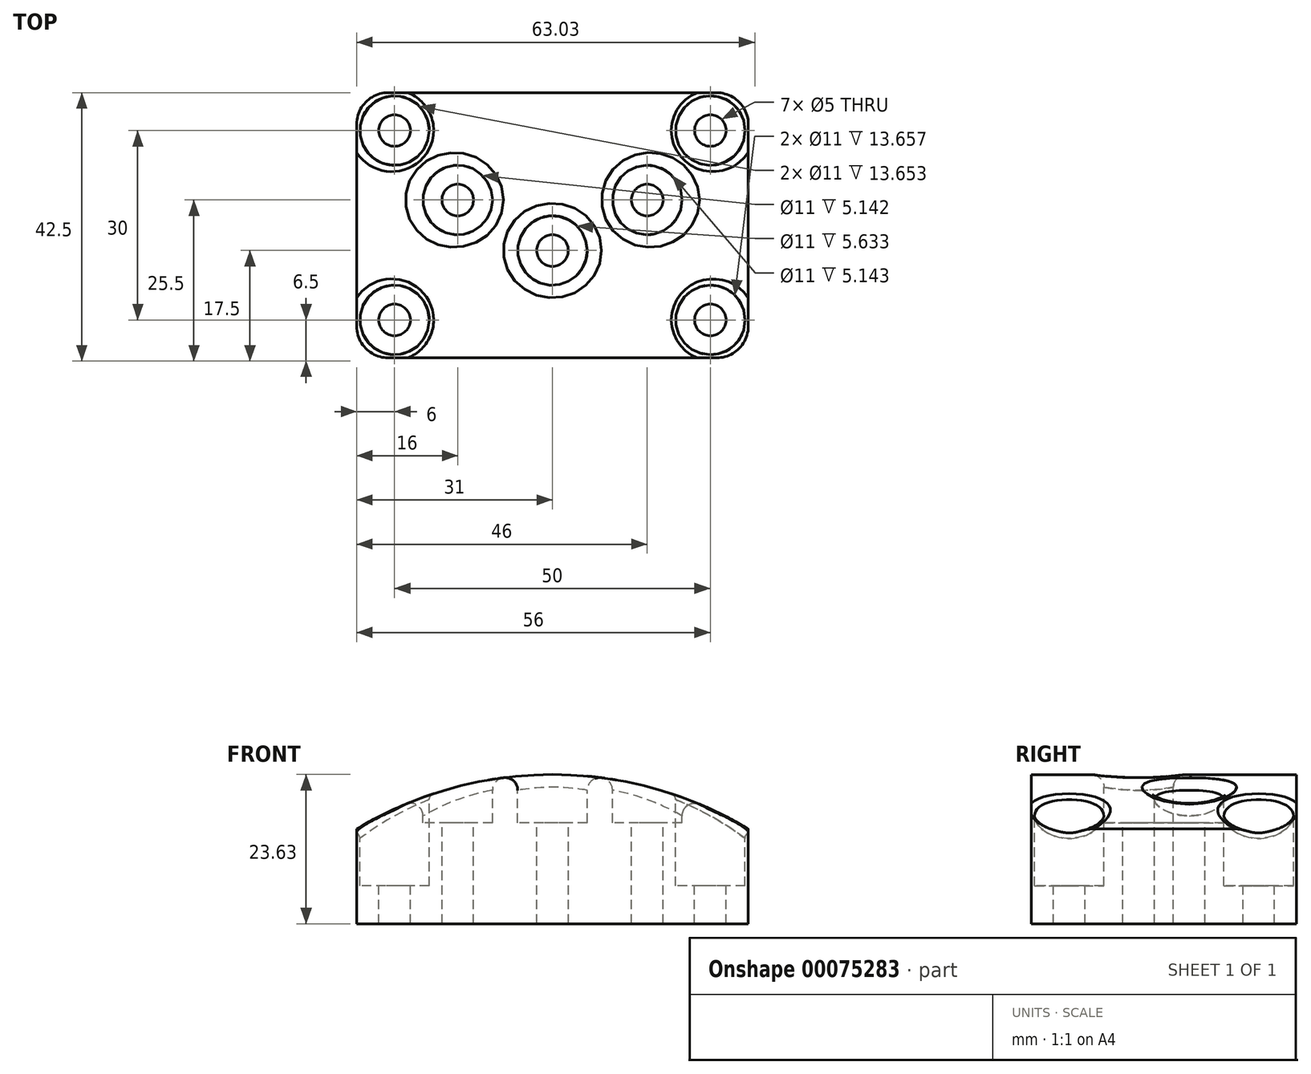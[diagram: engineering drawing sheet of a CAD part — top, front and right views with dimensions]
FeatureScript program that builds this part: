
annotation { "Feature Type Name" : "Feature", "Feature Type Description" : "" }
export const myFeature = defineFeature(function(context is Context, id is Id, definition is map)
    precondition{}
    {
        {
            var Q0;
            Q0=qCreatedBy(makeId("Top.planeOp"),FACE);
            var sketch = newSketch(context, id + "F0", { "sketchPlane" : qUnion([Q0])});
            skLineSegment(sketch, "E0.rect.bottom", {"start": v(-31, 21) * mm, "end": v(31, 21) * mm});
            skLineSegment(sketch, "E0.rect.top", {"start": v(-31, -21) * mm, "end": v(31, -21) * mm});
            skLineSegment(sketch, "E0.rect.left", {"start": v(-31, 21) * mm, "end": v(-31, -21) * mm});
            skLineSegment(sketch, "E0.rect.right", {"start": v(31, 21) * mm, "end": v(31, -21) * mm});
            skPoint(sketch, "E0.rect.middle", {"position": v(0, 0) * mm});
            skSolve(sketch);
        }
        {
            var Q0;
            Q0 = qSketchRegion(id + "F0", true);
            extrude(context, id + "F1", {"entities" : qUnion([Q0]), "depth" : 25 * mm});
        }
        {
            var Q0;
            Q0=makeQuery(id+"F1.opExtrude","CAP_FACE",FACE,{"disambiguationData":[OSD([sQuery(id+"F0.wireOp",EDGE,"E0.rect.bottom"),sQuery(id+"F0.wireOp",EDGE,"E0.rect.top"),sQuery(id+"F0.wireOp",EDGE,"E0.rect.left"),sQuery(id+"F0.wireOp",EDGE,"E0.rect.right")])],"isStart":false});
            var sketch = newSketch(context, id + "F2", { "sketchPlane" : qUnion([Q0])});
            skLineSegment(sketch, "E1", {"start": v(-25, 21) * mm, "end": v(-25, -21) * mm, "construction": true});
            skLineSegment(sketch, "E2", {"start": v(25, 21) * mm, "end": v(25, -21) * mm, "construction": true});
            skLineSegment(sketch, "E3", {"start": v(-31, -15) * mm, "end": v(31, -15) * mm, "construction": true});
            skLineSegment(sketch, "E4", {"start": v(-31, 15) * mm, "end": v(31, 15) * mm, "construction": true});
            skLineSegment(sketch, "E5", {"start": v(-31, 4) * mm, "end": v(31, 4) * mm, "construction": true});
            skLineSegment(sketch, "E6", {"start": v(-31, -4) * mm, "end": v(31, -4) * mm, "construction": true});
            skLineSegment(sketch, "E7", {"start": v(0, 21) * mm, "end": v(0, -21) * mm, "construction": true});
            skLineSegment(sketch, "E8", {"start": v(-15, 21) * mm, "end": v(-15, -21) * mm, "construction": true});
            skLineSegment(sketch, "E9", {"start": v(15, 21) * mm, "end": v(15, -21) * mm, "construction": true});
            skCircle(sketch, "E10", {"center": v(-25, 15) * mm, "radius": 2.5 * mm});
            skCircle(sketch, "E11", {"center": v(-25, -15) * mm, "radius": 2.5 * mm});
            skCircle(sketch, "E12", {"center": v(25, 15) * mm, "radius": 2.5 * mm});
            skCircle(sketch, "E13", {"center": v(0, -4) * mm, "radius": 2.5 * mm});
            skCircle(sketch, "E14", {"center": v(-15, 4) * mm, "radius": 2.5 * mm});
            skCircle(sketch, "E15", {"center": v(15, 4) * mm, "radius": 2.5 * mm});
            skCircle(sketch, "E16", {"center": v(25, -15) * mm, "radius": 2.5 * mm});
            skSolve(sketch);
        }
        {
            var Q0;
            Q0 = qSketchRegion(id + "F2", true);
            var Q1;
            Q1=makeQuery(id+"F1.opExtrude","CAP_FACE",FACE,{"disambiguationData":[OSD([sQuery(id+"F0.wireOp",EDGE,"E0.rect.bottom"),sQuery(id+"F0.wireOp",EDGE,"E0.rect.top"),sQuery(id+"F0.wireOp",EDGE,"E0.rect.left"),sQuery(id+"F0.wireOp",EDGE,"E0.rect.right")])],"isStart":true});
            extrude(context, id + "F3", {"entities" : qUnion([Q0]), "operationType" : NewBodyOperationType.REMOVE, "endBound" : BoundingType.UP_TO_SURFACE, "oppositeDirection" : true, "endBoundEntityFace" : qUnion([Q1]), "depth" : 25 * mm});
        }
        {
            var Q0;
            Q0=makeQuery(id+"F1.opExtrude","CAP_FACE",FACE,{"disambiguationData":[OSD([sQuery(id+"F0.wireOp",EDGE,"E0.rect.bottom"),sQuery(id+"F0.wireOp",EDGE,"E0.rect.top"),sQuery(id+"F0.wireOp",EDGE,"E0.rect.left"),sQuery(id+"F0.wireOp",EDGE,"E0.rect.right")])],"isStart":false});
            var sketch = newSketch(context, id + "F4", { "sketchPlane" : qUnion([Q0])});
            skCircle(sketch, "E17", {"center": v(-15, 4) * mm, "radius": 5.5 * mm});
            skCircle(sketch, "E18", {"center": v(0, -4) * mm, "radius": 5.5 * mm});
            skCircle(sketch, "E19", {"center": v(15, 4) * mm, "radius": 5.5 * mm});
            skSolve(sketch);
        }
        {
            var Q0;
            Q0 = qSketchRegion(id + "F4", true);
            extrude(context, id + "F5", {"entities" : qUnion([Q0]), "operationType" : NewBodyOperationType.REMOVE, "oppositeDirection" : true, "depth" : 9 * mm});
        }
        {
            var Q0;
            Q0=makeQuery(id+"F1.opExtrude","CAP_FACE",FACE,{"disambiguationData":[OSD([sQuery(id+"F0.wireOp",EDGE,"E0.rect.bottom"),sQuery(id+"F0.wireOp",EDGE,"E0.rect.top"),sQuery(id+"F0.wireOp",EDGE,"E0.rect.left"),sQuery(id+"F0.wireOp",EDGE,"E0.rect.right")])],"isStart":false});
            var sketch = newSketch(context, id + "F6", { "sketchPlane" : qUnion([Q0])});
            skCircle(sketch, "E20", {"center": v(-25, 15) * mm, "radius": 5.5 * mm});
            skCircle(sketch, "E21", {"center": v(25, 15) * mm, "radius": 5.5 * mm});
            skCircle(sketch, "E22", {"center": v(25, -15) * mm, "radius": 5.5 * mm});
            skCircle(sketch, "E23", {"center": v(-25, -15) * mm, "radius": 5.5 * mm});
            skSolve(sketch);
        }
        {
            var Q0;
            Q0 = qSketchRegion(id + "F6", true);
            extrude(context, id + "F7", {"entities" : qUnion([Q0]), "operationType" : NewBodyOperationType.REMOVE, "oppositeDirection" : true, "depth" : 19 * mm});
        }
        {
            var Q0;
            Q0=makeQuery(id+"F1.opExtrude","SWEPT_FACE",FACE,{"disambiguationData":[OSD([sQuery(id+"F0.wireOp",EDGE,"E0.rect.top")])]});
            var sketch = newSketch(context, id + "F8", { "sketchPlane" : qUnion([Q0])});
            skArc(sketch, "E24", {"start": v(31, 15) * mm, "mid": v(0, 23.63) * mm, "end": v(-31, 15) * mm});
            skLineSegment(sketch, "E25", {"start": v(-31, 15) * mm, "end": v(-53.05, 15) * mm});
            skLineSegment(sketch, "E26", {"start": v(-53.05, 15) * mm, "end": v(-53.05, 56.68) * mm});
            skLineSegment(sketch, "E27", {"start": v(-53.05, 56.68) * mm, "end": v(46.39, 56.68) * mm});
            skLineSegment(sketch, "E28", {"start": v(46.39, 56.68) * mm, "end": v(46.39, 15) * mm});
            skLineSegment(sketch, "E29", {"start": v(46.39, 15) * mm, "end": v(31, 15) * mm});
            skSolve(sketch);
        }
        {
            var Q0;
            Q0 = qSketchRegion(id + "F8", true);
            var Q1;
            Q1=makeQuery(id+"F1.opExtrude","SWEPT_FACE",FACE,{"disambiguationData":[OSD([sQuery(id+"F0.wireOp",EDGE,"E0.rect.bottom")])]});
            extrude(context, id + "F9", {"entities" : qUnion([Q0]), "operationType" : NewBodyOperationType.REMOVE, "endBound" : BoundingType.UP_TO_SURFACE, "oppositeDirection" : true, "endBoundEntityFace" : qUnion([Q1]), "depth" : 25 * mm});
        }
        {
            var Q0;
            Q0=makeQuery(id+"F1.opExtrude","SWEPT_EDGE",EDGE,{"disambiguationData":[OSD([sQuery(id+"F0.wireOp",EDGE,"E0.rect.top"),sQuery(id+"F0.wireOp",EDGE,"E0.rect.left")])]});
            var Q1;
            Q1=makeQuery(id+"F1.opExtrude","SWEPT_EDGE",EDGE,{"disambiguationData":[OSD([sQuery(id+"F0.wireOp",EDGE,"E0.rect.bottom"),sQuery(id+"F0.wireOp",EDGE,"E0.rect.left")])]});
            var Q2;
            Q2=makeQuery(id+"F1.opExtrude","SWEPT_EDGE",EDGE,{"disambiguationData":[OSD([sQuery(id+"F0.wireOp",EDGE,"E0.rect.top"),sQuery(id+"F0.wireOp",EDGE,"E0.rect.right")])]});
            var Q3;
            Q3=makeQuery(id+"F1.opExtrude","SWEPT_EDGE",EDGE,{"disambiguationData":[OSD([sQuery(id+"F0.wireOp",EDGE,"E0.rect.bottom"),sQuery(id+"F0.wireOp",EDGE,"E0.rect.right")])]});
            fillet(context, id + "F10", {"entities" : qUnion([Q0, Q1, Q2, Q3]), "radius" : 5 * mm, "tangentPropagation" : true, "allowEdgeOverflow" : false});
        }
        {
            var Q0;
            Q0=makeQuery(id+"F9.boolean.opBoolean","INTERSECT",EDGE,{"derivedFrom":[makeQuery(id+"F5.boolean.opBoolean","COPY",FACE,{"derivedFrom":makeQuery(id+"F5.opExtrude","SWEPT_FACE",FACE,{"disambiguationData":[OSD([sQuery(id+"F4.wireOp",EDGE,"E18")])]})}),makeQuery(id+"F9.opExtrude","SWEPT_FACE",FACE,{"disambiguationData":[OSD([sQuery(id+"F8.wireOp",EDGE,"E24")])]})]});
            var Q1;
            Q1=makeQuery(id+"F9.boolean.opBoolean","INTERSECT",EDGE,{"derivedFrom":[makeQuery(id+"F5.boolean.opBoolean","COPY",FACE,{"derivedFrom":makeQuery(id+"F5.opExtrude","SWEPT_FACE",FACE,{"disambiguationData":[OSD([sQuery(id+"F4.wireOp",EDGE,"E19")])]})}),makeQuery(id+"F9.opExtrude","SWEPT_FACE",FACE,{"disambiguationData":[OSD([sQuery(id+"F8.wireOp",EDGE,"E24")])]})]});
            var Q2;
            Q2=makeQuery(id+"F9.boolean.opBoolean","INTERSECT",EDGE,{"derivedFrom":[makeQuery(id+"F5.boolean.opBoolean","COPY",FACE,{"derivedFrom":makeQuery(id+"F5.opExtrude","SWEPT_FACE",FACE,{"disambiguationData":[OSD([sQuery(id+"F4.wireOp",EDGE,"E17")])]})}),makeQuery(id+"F9.opExtrude","SWEPT_FACE",FACE,{"disambiguationData":[OSD([sQuery(id+"F8.wireOp",EDGE,"E24")])]})]});
            fillet(context, id + "F11", {"entities" : qUnion([Q0, Q1, Q2]), "radius" : 2 * mm, "tangentPropagation" : true, "allowEdgeOverflow" : false});
        }
        {
            var Q0;
            Q0=makeQuery(id+"F9.boolean.opBoolean","INTERSECT",EDGE,{"derivedFrom":[makeQuery(id+"F7.boolean.opBoolean","COPY",FACE,{"derivedFrom":makeQuery(id+"F7.opExtrude","SWEPT_FACE",FACE,{"disambiguationData":[OSD([sQuery(id+"F6.wireOp",EDGE,"E22")])]})}),makeQuery(id+"F9.opExtrude","SWEPT_FACE",FACE,{"disambiguationData":[OSD([sQuery(id+"F8.wireOp",EDGE,"E24")])]})]});
            var Q1;
            Q1=makeQuery(id+"F9.boolean.opBoolean","INTERSECT",EDGE,{"derivedFrom":[makeQuery(id+"F7.boolean.opBoolean","COPY",FACE,{"derivedFrom":makeQuery(id+"F7.opExtrude","SWEPT_FACE",FACE,{"disambiguationData":[OSD([sQuery(id+"F6.wireOp",EDGE,"E21")])]})}),makeQuery(id+"F9.opExtrude","SWEPT_FACE",FACE,{"disambiguationData":[OSD([sQuery(id+"F8.wireOp",EDGE,"E24")])]})]});
            var Q2;
            Q2=makeQuery(id+"F9.boolean.opBoolean","INTERSECT",EDGE,{"derivedFrom":[makeQuery(id+"F7.boolean.opBoolean","COPY",FACE,{"derivedFrom":makeQuery(id+"F7.opExtrude","SWEPT_FACE",FACE,{"disambiguationData":[OSD([sQuery(id+"F6.wireOp",EDGE,"E20")])]})}),makeQuery(id+"F9.opExtrude","SWEPT_FACE",FACE,{"disambiguationData":[OSD([sQuery(id+"F8.wireOp",EDGE,"E24")])]})]});
            var Q3;
            Q3=makeQuery(id+"F9.boolean.opBoolean","INTERSECT",EDGE,{"derivedFrom":[makeQuery(id+"F7.boolean.opBoolean","COPY",FACE,{"derivedFrom":makeQuery(id+"F7.opExtrude","SWEPT_FACE",FACE,{"disambiguationData":[OSD([sQuery(id+"F6.wireOp",EDGE,"E23")])]})}),makeQuery(id+"F9.opExtrude","SWEPT_FACE",FACE,{"disambiguationData":[OSD([sQuery(id+"F8.wireOp",EDGE,"E24")])]})]});
            fillet(context, id + "F12", {"entities" : qUnion([Q0, Q1, Q2, Q3]), "radius" : 1 * mm, "tangentPropagation" : true, "allowEdgeOverflow" : false});
        }
    });
